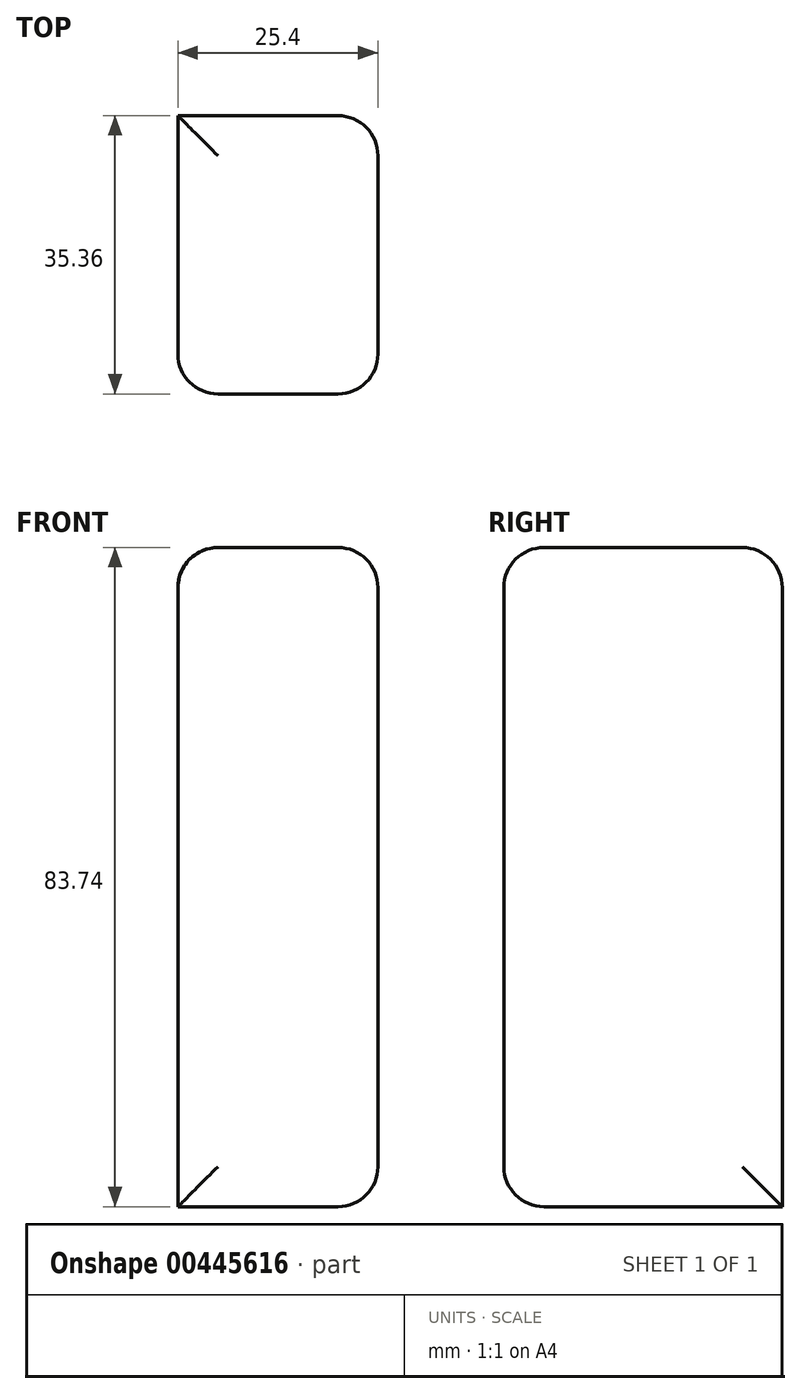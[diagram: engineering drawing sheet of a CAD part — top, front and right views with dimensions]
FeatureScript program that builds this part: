
annotation { "Feature Type Name" : "Feature", "Feature Type Description" : "" }
export const myFeature = defineFeature(function(context is Context, id is Id, definition is map)
    precondition{}
    {
        {
            var Q0;
            Q0=qCreatedBy(makeId("Right.planeOp"),FACE);
            var sketch = newSketch(context, id + "F0", { "sketchPlane" : qUnion([Q0])});
            skLineSegment(sketch, "E0.bottom", {"start": v(17.68, 41.87) * mm, "end": v(-17.68, 41.87) * mm});
            skLineSegment(sketch, "E0.top", {"start": v(17.68, -41.87) * mm, "end": v(-17.68, -41.87) * mm});
            skLineSegment(sketch, "E0.left", {"start": v(17.68, 41.87) * mm, "end": v(17.68, -41.87) * mm});
            skLineSegment(sketch, "E0.right", {"start": v(-17.68, 41.87) * mm, "end": v(-17.68, -41.87) * mm});
            skPoint(sketch, "E0.middle", {"position": v(0, 0) * mm});
            skSolve(sketch);
        }
        {
            var Q0;
            Q0=makeQuery(id+"F0.imprint","IMPRINT",FACE,{"disambiguationData":[TD([[makeQuery(id+"F0.imprint","IMPRINT",EDGE,{"derivedFrom":sQuery(id+"F0.wireOp",EDGE,"E0.bottom")}),1.0]])]});
            extrude(context, id + "F1", {"entities" : qUnion([Q0]), "depth" : 25.4 * mm});
        }
        {
            var Q0;
            Q0=makeQuery(id+"F1.opExtrude","SWEPT_EDGE",EDGE,{"disambiguationData":[OSD([sQuery(id+"F0.wireOp",EDGE,"E0.bottom"),sQuery(id+"F0.wireOp",EDGE,"E0.right")])]});
            var Q1;
            Q1=makeQuery(id+"F1.opExtrude","CAP_EDGE",EDGE,{"disambiguationData":[OSD([sQuery(id+"F0.wireOp",EDGE,"E0.bottom")])],"isStart":false});
            var Q2;
            Q2=makeQuery(id+"F1.opExtrude","SWEPT_EDGE",EDGE,{"disambiguationData":[OSD([sQuery(id+"F0.wireOp",EDGE,"E0.bottom"),sQuery(id+"F0.wireOp",EDGE,"E0.left")])]});
            var Q3;
            Q3=makeQuery(id+"F1.opExtrude","CAP_EDGE",EDGE,{"disambiguationData":[OSD([sQuery(id+"F0.wireOp",EDGE,"E0.bottom")])],"isStart":true});
            var Q4;
            Q4=makeQuery(id+"F1.opExtrude","CAP_EDGE",EDGE,{"disambiguationData":[OSD([sQuery(id+"F0.wireOp",EDGE,"E0.right")])],"isStart":false});
            var Q5;
            Q5=makeQuery(id+"F1.opExtrude","CAP_EDGE",EDGE,{"disambiguationData":[OSD([sQuery(id+"F0.wireOp",EDGE,"E0.left")])],"isStart":false});
            var Q6;
            Q6=makeQuery(id+"F1.opExtrude","CAP_EDGE",EDGE,{"disambiguationData":[OSD([sQuery(id+"F0.wireOp",EDGE,"E0.right")])],"isStart":true});
            var Q7;
            Q7=makeQuery(id+"F1.opExtrude","SWEPT_EDGE",EDGE,{"disambiguationData":[OSD([sQuery(id+"F0.wireOp",EDGE,"E0.top"),sQuery(id+"F0.wireOp",EDGE,"E0.right")])]});
            var Q8;
            Q8=makeQuery(id+"F1.opExtrude","CAP_FACE",FACE,{"disambiguationData":[OSD([sQuery(id+"F0.wireOp",EDGE,"E0.bottom"),sQuery(id+"F0.wireOp",EDGE,"E0.top"),sQuery(id+"F0.wireOp",EDGE,"E0.left"),sQuery(id+"F0.wireOp",EDGE,"E0.right")])],"isStart":false});
            fillet(context, id + "F2", {"entities" : qUnion([Q0, Q1, Q2, Q3, Q4, Q5, Q6, Q7, Q8]), "radius" : 5.08 * mm, "tangentPropagation" : true, "allowEdgeOverflow" : false});
        }
    });
